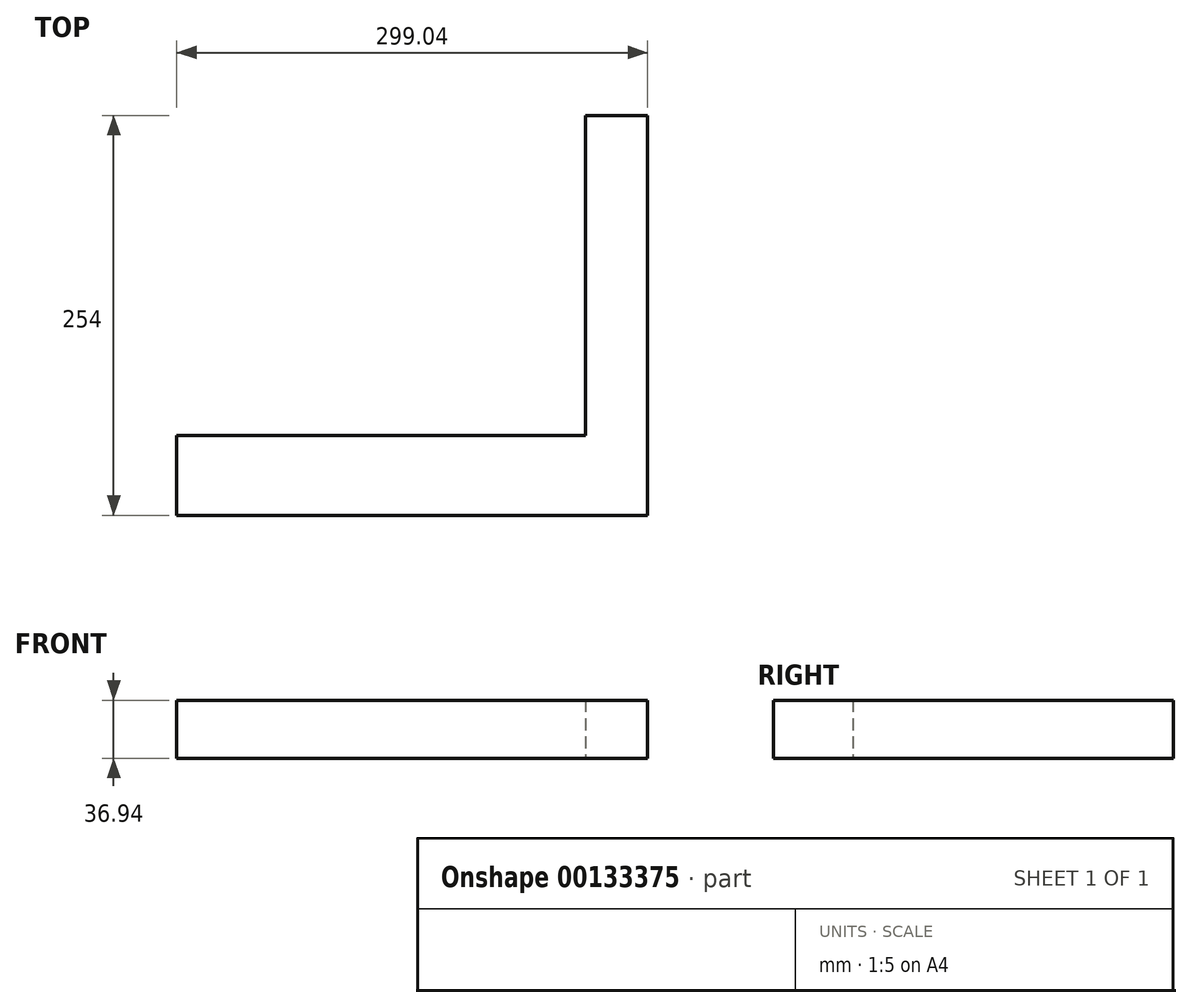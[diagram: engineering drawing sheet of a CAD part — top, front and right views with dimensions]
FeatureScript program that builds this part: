
annotation { "Feature Type Name" : "Feature", "Feature Type Description" : "" }
export const myFeature = defineFeature(function(context is Context, id is Id, definition is map)
    precondition{}
    {
        {
            var Q0;
            Q0=qCreatedBy(makeId("Front.planeOp"),FACE);
            var sketch = newSketch(context, id + "F0", { "sketchPlane" : qUnion([Q0])});
            skLineSegment(sketch, "E0.bottom", {"start": v(0, 0) * mm, "end": v(39.36, 0) * mm});
            skLineSegment(sketch, "E0.top", {"start": v(0, 36.94) * mm, "end": v(39.36, 36.94) * mm});
            skLineSegment(sketch, "E0.left", {"start": v(0, 0) * mm, "end": v(0, 36.94) * mm});
            skLineSegment(sketch, "E0.right", {"start": v(39.36, 0) * mm, "end": v(39.36, 36.94) * mm});
            skSolve(sketch);
        }
        {
            var Q0;
            Q0=makeQuery(id+"F0.imprint","IMPRINT",FACE,{"disambiguationData":[TD([[makeQuery(id+"F0.imprint","IMPRINT",EDGE,{"derivedFrom":sQuery(id+"F0.wireOp",EDGE,"E0.bottom")}),1.0]])]});
            extrude(context, id + "F1", {"entities" : qUnion([Q0]), "depth" : 254 * mm});
        }
        {
            var Q0;
            Q0=makeQuery(id+"F1.opExtrude","SWEPT_FACE",FACE,{"disambiguationData":[OSD([sQuery(id+"F0.wireOp",EDGE,"E0.left")])]});
            var sketch = newSketch(context, id + "F2", { "sketchPlane" : qUnion([Q0])});
            skLineSegment(sketch, "E1.bottom", {"start": v(254, 36.94) * mm, "end": v(203.44, 36.94) * mm});
            skLineSegment(sketch, "E1.top", {"start": v(254, 0) * mm, "end": v(203.44, 0) * mm});
            skLineSegment(sketch, "E1.left", {"start": v(254, 36.94) * mm, "end": v(254, 0) * mm});
            skLineSegment(sketch, "E1.right", {"start": v(203.44, 36.94) * mm, "end": v(203.44, 0) * mm});
            skSolve(sketch);
        }
        {
            var Q0;
            Q0=makeQuery(id+"F2.imprint","IMPRINT",FACE,{"disambiguationData":[TD([[makeQuery(id+"F2.imprint","IMPRINT",EDGE,{"derivedFrom":sQuery(id+"F2.wireOp",EDGE,"E1.bottom")}),1.0]])]});
            extrude(context, id + "F3", {"entities" : qUnion([Q0]), "operationType" : NewBodyOperationType.ADD, "endBound" : BoundingType.THROUGH_ALL, "depth" : 25.4 * mm});
        }
    });
